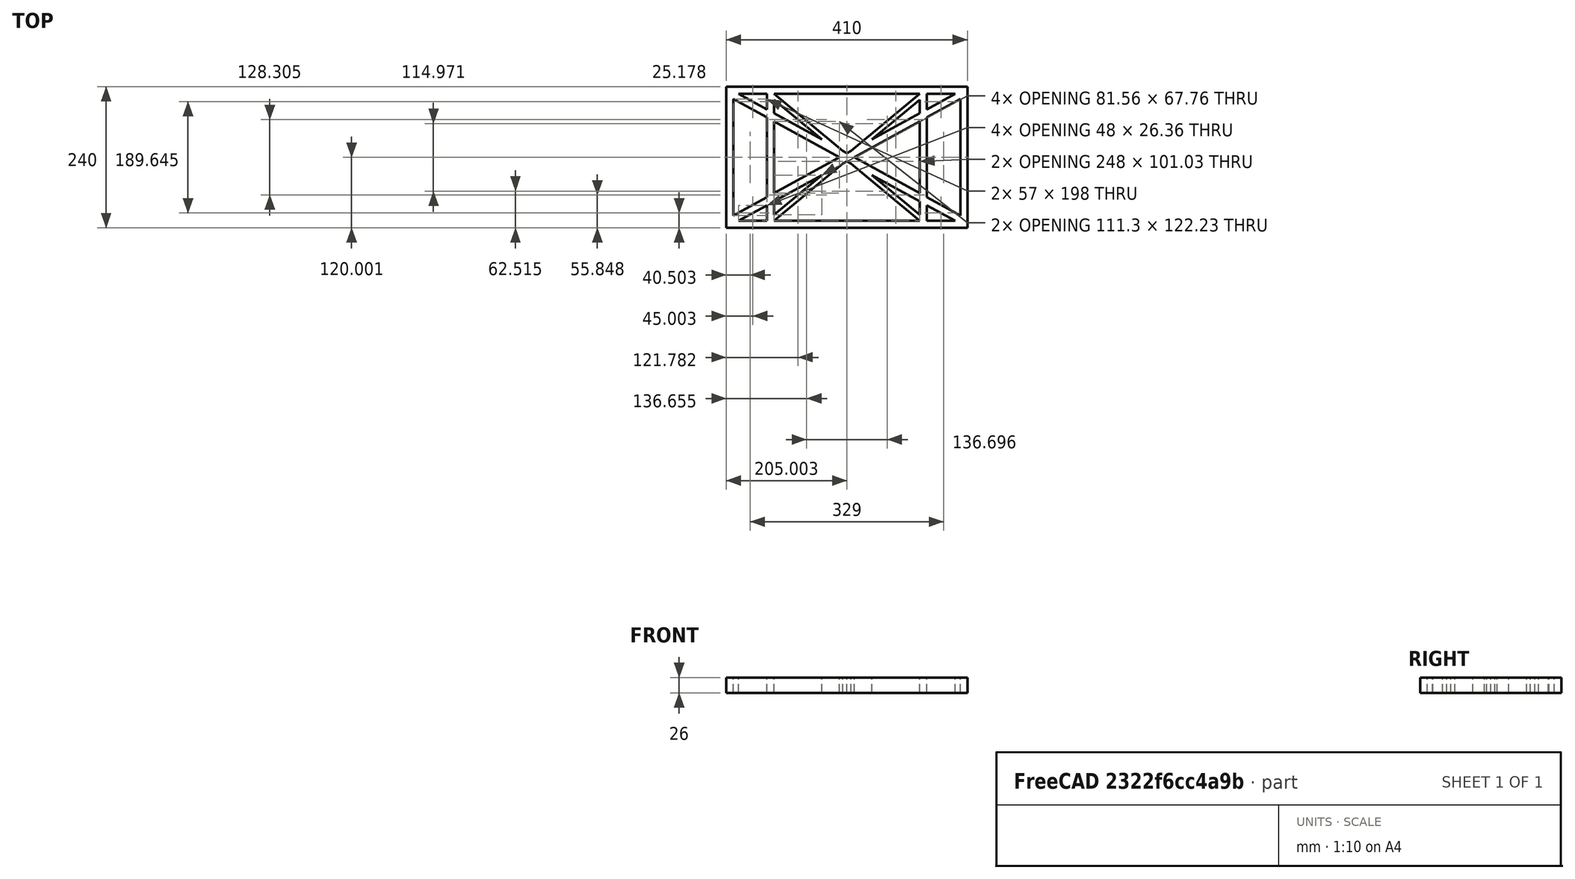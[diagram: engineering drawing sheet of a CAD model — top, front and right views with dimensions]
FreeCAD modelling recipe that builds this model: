
FCSTD DOCUMENT  (FreeCAD 0.19R0.19.2)
Label: laptopStand035
License: All rights reserved
LicenseURL: http://en.wikipedia.org/wiki/All_rights_reserved
objects: Sketcher::SketchObject×2, Part::Extrusion×1
note: 3 computed .brp shape members not serialized (recipe doc carries the construction recipe); baked Part::Feature solids carry a one-line shape summary decoded from their .brp

FEATURE [Sketcher::SketchObject] Sketch
  FullyConstrained = true
  sketch-geometry (52):
    g0: LineSegment StartX=-22.9272 StartY=136.221 StartZ=0 EndX=-22.9272 EndY=-103.779 EndZ=0
    g1: LineSegment StartX=-22.9272 StartY=136.221 StartZ=0 EndX=387.073 EndY=136.221 EndZ=0
    g2: LineSegment StartX=-22.9272 StartY=-103.779 StartZ=0 EndX=387.073 EndY=-103.779 EndZ=0
    g3: LineSegment StartX=387.073 StartY=136.221 StartZ=0 EndX=387.073 EndY=-103.779 EndZ=0
    g4: LineSegment StartX=375.073 StartY=115.221 StartZ=0 EndX=318.073 EndY=83.9235 EndZ=0
    g5: LineSegment StartX=-10.9272 StartY=-82.7794 StartZ=0 EndX=46.0728 EndY=-51.4823 EndZ=0
    g6: LineSegment StartX=-1.92719 StartY=124.221 StartZ=0 EndX=46.0728 EndY=97.8651 EndZ=0
    g7: LineSegment StartX=366.073 StartY=-91.7794 StartZ=0 EndX=318.073 EndY=-65.424 EndZ=0
    g8: LineSegment StartX=-10.9272 StartY=115.221 StartZ=0 EndX=-10.9272 EndY=-82.7794 EndZ=0
    g9: LineSegment StartX=375.073 StartY=-82.7794 StartZ=0 EndX=375.073 EndY=115.221 EndZ=0
    g10: LineSegment StartX=-1.92719 StartY=-91.7794 StartZ=0 EndX=46.0728 EndY=-91.7794 EndZ=0
    g11: LineSegment StartX=318.073 StartY=124.221 StartZ=0 EndX=366.073 EndY=124.221 EndZ=0
    g12: LineSegment StartX=306.073 StartY=-81.8102 StartZ=0 EndX=224.513 EndY=-14.0532 EndZ=0
    g13: LineSegment StartX=58.0728 StartY=114.251 StartZ=0 EndX=139.632 EndY=46.4944 EndZ=0
    g14: LineSegment StartX=306.073 StartY=124.221 StartZ=0 EndX=189.124 EndY=27.0628 EndZ=0
    g15: LineSegment StartX=58.0728 StartY=-91.7794 StartZ=0 EndX=175.022 EndY=5.37834 EndZ=0
    g16: LineSegment StartX=46.0728 StartY=124.221 StartZ=0 EndX=46.0728 EndY=97.8651 EndZ=0
    g17: LineSegment StartX=58.0728 StartY=-81.8102 StartZ=0 EndX=58.0728 EndY=-58.8351 EndZ=0
    g18: LineSegment StartX=318.073 StartY=124.221 StartZ=0 EndX=318.073 EndY=97.8651 EndZ=0
    g19: LineSegment StartX=306.073 StartY=114.251 StartZ=0 EndX=306.073 EndY=91.2763 EndZ=0
    g20: LineSegment StartX=182.073 StartY=23.1914 StartZ=0 EndX=189.124 EndY=27.0628 EndZ=0
    g21: LineSegment StartX=182.073 StartY=9.24976 StartZ=0 EndX=175.022 EndY=5.37834 EndZ=0
    g22: LineSegment StartX=224.513 StartY=46.4944 StartZ=0 EndX=306.073 EndY=114.251 EndZ=0
    g23: LineSegment StartX=175.022 StartY=27.0628 StartZ=0 EndX=58.0728 EndY=124.221 EndZ=0
    g24: LineSegment StartX=169.377 StartY=16.2206 StartZ=0 EndX=58.0728 EndY=77.3346 EndZ=0
    g25: LineSegment StartX=139.632 StartY=-14.0532 StartZ=0 EndX=58.0728 EndY=-81.8102 EndZ=0
    g26: LineSegment StartX=194.768 StartY=16.2206 StartZ=0 EndX=306.073 EndY=-44.8935 EndZ=0
    g27: LineSegment StartX=224.513 StartY=46.4944 StartZ=0 EndX=306.073 EndY=91.2763 EndZ=0
    g28: LineSegment StartX=175.022 StartY=27.0628 StartZ=0 EndX=182.073 EndY=23.1914 EndZ=0
    g29: LineSegment StartX=139.632 StartY=-14.0532 StartZ=0 EndX=58.0728 EndY=-58.8351 EndZ=0
    g30: LineSegment StartX=189.124 StartY=5.37834 StartZ=0 EndX=182.073 EndY=9.24976 EndZ=0
    g31: LineSegment StartX=189.124 StartY=5.37834 StartZ=0 EndX=306.073 EndY=-91.7794 EndZ=0
    g32: LineSegment StartX=306.073 StartY=77.3346 StartZ=0 EndX=306.073 EndY=-44.8935 EndZ=0
    g33: LineSegment StartX=318.073 StartY=83.9235 StartZ=0 EndX=318.073 EndY=-51.4823 EndZ=0
    g34: LineSegment StartX=318.073 StartY=97.8651 StartZ=0 EndX=366.073 EndY=124.221 EndZ=0
    g35: LineSegment StartX=306.073 StartY=77.3346 StartZ=0 EndX=194.768 EndY=16.2206 EndZ=0
    g36: LineSegment StartX=306.073 StartY=-58.8351 StartZ=0 EndX=224.513 EndY=-14.0532 EndZ=0
    g37: LineSegment StartX=306.073 StartY=-58.8351 StartZ=0 EndX=306.073 EndY=-81.8102 EndZ=0
    g38: LineSegment StartX=318.073 StartY=-51.4823 StartZ=0 EndX=375.073 EndY=-82.7794 EndZ=0
    g39: LineSegment StartX=318.073 StartY=-65.424 StartZ=0 EndX=318.073 EndY=-91.7794 EndZ=0
    g40: LineSegment StartX=306.073 StartY=124.221 StartZ=0 EndX=58.0728 EndY=124.221 EndZ=0
    g41: LineSegment StartX=318.073 StartY=-91.7794 StartZ=0 EndX=366.073 EndY=-91.7794 EndZ=0
    g42: LineSegment StartX=58.0728 StartY=-91.7794 StartZ=0 EndX=306.073 EndY=-91.7794 EndZ=0
    g43: LineSegment StartX=58.0728 StartY=-44.8935 StartZ=0 EndX=58.0728 EndY=77.3346 EndZ=0
    g44: LineSegment StartX=46.0728 StartY=-65.424 StartZ=0 EndX=-1.92719 EndY=-91.7794 EndZ=0
    g45: LineSegment StartX=46.0728 StartY=-65.424 StartZ=0 EndX=46.0728 EndY=-91.7794 EndZ=0
    g46: LineSegment StartX=58.0728 StartY=-44.8935 StartZ=0 EndX=169.377 EndY=16.2206 EndZ=0
    g47: LineSegment StartX=58.0728 StartY=91.2763 StartZ=0 EndX=58.0728 EndY=114.251 EndZ=0
    g48: LineSegment StartX=46.0728 StartY=83.9235 StartZ=0 EndX=46.0728 EndY=-51.4823 EndZ=0
    g49: LineSegment StartX=46.0728 StartY=124.221 StartZ=0 EndX=-1.92719 EndY=124.221 EndZ=0
    g50: LineSegment StartX=58.0728 StartY=91.2763 StartZ=0 EndX=139.632 EndY=46.4944 EndZ=0
    g51: LineSegment StartX=46.0728 StartY=83.9235 StartZ=0 EndX=-10.9272 EndY=115.221 EndZ=0
  constraints (102):
    c: Vertical(g0)
    c: Distance(g0) = 240
    c: Horizontal(g1)
    c: Distance(g1) = 410
    c: Coincident(g1,g0)
    c: Coincident(g2,g0)
    c: Horizontal(g2)
    c: Coincident(g3,g1)
    c: Vertical(g3)
    c: Coincident(g2,g3)
    c: Block(g1)
    c: Horizontal(g10)
    c: Horizontal(g11)
    c: PointOnObject(g35,g6)
    c: Coincident(g28,g20)
    c: Coincident(g30,g21)
    c: Tangent(g7,g24)
    c: PointOnObject(g24,g5)
    c: PointOnObject(g26,g4)
    c: Coincident(g20,g14)
    c: Tangent(g20,g27)
    c: Coincident(g50,g13)
    c: Coincident(g28,g23)
    c: Coincident(g22,g27)
    c: Coincident(g21,g15)
    c: Coincident(g29,g25)
    c: Tangent(g21,g29)
    c: Coincident(g36,g12)
    c: Coincident(g31,g30)
    c: Coincident(g22,g19)
    c: Tangent(g19,g32)
    c: Tangent(g18,g33)
    c: Coincident(g27,g19)
    c: Tangent(g27,g34)
    c: Coincident(g4,g33)
    c: Coincident(g35,g32)
    c: Tangent(g4,g35)
    c: Coincident(g37,g12)
    c: Tangent(g7,g36)
    c: Tangent(g32,g37)
    c: Coincident(g26,g32)
    c: Tangent(g26,g38)
    c: Coincident(g33,g38)
    c: Coincident(g39,g7)
    c: Tangent(g33,g39)
    c: Coincident(g25,g17)
    c: Tangent(g17,g43)
    c: Coincident(g29,g17)
    c: Tangent(g29,g44)
    c: Coincident(g45,g44)
    c: Tangent(g16,g45)
    c: Coincident(g5,g48)
    c: Coincident(g46,g43)
    c: Tangent(g5,g46)
    c: Tangent(g43,g47)
    c: Tangent(g16,g48)
    c: Coincident(g13,g47)
    c: PointOnObject(g40,g23)
    c: Tangent(g40,g49)
    c: Coincident(g6,g16)
    c: Coincident(g50,g47)
    c: Tangent(g6,g50)
    c: Coincident(g24,g43)
    c: Coincident(g51,g48)
    c: Tangent(g24,g51)
    c: Block(g23)
    c: Block(g14)
    c: Block(g20)
    c: Block(g40)
    c: Block(g18)
    c: Block(g34)
    c: Block(g4)
    c: Block(g38)
    c: Block(g9)
    c: Block(g36)
    c: Block(g37)
    c: Block(g7)
    c: Block(g39)
    c: Block(g22)
    c: Block(g31)
    c: Block(g42)
    c: Block(g21)
    c: Block(g15)
    c: Block(g29)
    c: Block(g25)
    c: Block(g45)
    c: Block(g44)
    c: Block(g5)
    c: Block(g8)
    c: Block(g51)
    c: Block(g6)
    c: Block(g16)
    c: Block(g13)
    c: Block(g47)
    c: Block(g35)
    c: Block(g32)
    c: Block(g24)
    c: Block(g46)
    c: Block(g49)
    c: Block(g11)
    c: Block(g41)
    c: Block(g10)
FEATURE [Part::Extrusion] Extrude
  Base = -> Sketch
  Dir = (0,0,1)
  DirMode = 2
  FaceMakerClass = Part::FaceMakerBullseye
  LengthFwd = 26
  LengthRev = 0
  Solid = true
  Symmetric = false
FEATURE [Sketcher::SketchObject] Sketch001
  FullyConstrained = true
  MapMode = 4
  Placement = pos=(0,0,0) rot=(0.57735,0.57735,0.57735;2.0944rad)
  Support = -> [Sketch]
  sketch-geometry (46):
    g0: BSplineCurve PolesCount=3 KnotsCount=2 Degree=2 IsPeriodic=0
    g1: ArcOfCircle CenterX=73.122 CenterY=-32.2909 CenterZ=0 NormalX=0 NormalY=0 NormalZ=1 AngleXU=0 Radius=13 StartAngle=5.92268 EndAngle=9.06428
    g2: LineSegment StartX=85.2864 StartY=-36.8765 StartZ=0 EndX=78.9505 EndY=-53.7246 EndZ=0
    g3: LineSegment StartX=60.9577 StartY=-27.7052 StartZ=0 EndX=54.6191 EndY=-44.5532 EndZ=0
    g4: ArcOfCircle CenterX=66.7816 CenterY=-49.1439 CenterZ=0 NormalX=0 NormalY=0 NormalZ=1 AngleXU=0 Radius=13 StartAngle=2.78068 EndAngle=5.92131
    g5: ArcOfCircle CenterX=55.9263 CenterY=-78.1807 CenterZ=0 NormalX=0 NormalY=0 NormalZ=1 AngleXU=0 Radius=13 StartAngle=5.92268 EndAngle=9.06428
    g6: LineSegment StartX=68.0907 StartY=-82.7664 StartZ=0 EndX=61.7547 EndY=-99.6148 EndZ=0
    g7: ArcOfCircle CenterX=49.5884 CenterY=-95.0342 CenterZ=0 NormalX=0 NormalY=0 NormalZ=1 AngleXU=0 Radius=13 StartAngle=2.78068 EndAngle=5.92131
    g8: LineSegment StartX=43.7619 StartY=-73.595 StartZ=0 EndX=37.426 EndY=-90.4435 EndZ=0
    g9: ArcOfCircle CenterX=38.7206 CenterY=-124.067 CenterZ=0 NormalX=0 NormalY=0 NormalZ=1 AngleXU=0 Radius=13 StartAngle=5.92268 EndAngle=9.06428
    g10: LineSegment StartX=26.5562 StartY=-119.481 StartZ=0 EndX=20.2251 EndY=-136.329 EndZ=0
    g11: ArcOfCircle CenterX=32.3875 CenterY=-140.92 CenterZ=0 NormalX=0 NormalY=0 NormalZ=1 AngleXU=0 Radius=13 StartAngle=2.78068 EndAngle=5.92131
    g12: LineSegment StartX=50.885 StartY=-128.652 StartZ=0 EndX=44.549 EndY=-145.5 EndZ=0
    g13: ArcOfCircle CenterX=21.4715 CenterY=-169.934 CenterZ=0 NormalX=0 NormalY=0 NormalZ=1 AngleXU=0 Radius=13 StartAngle=5.92268 EndAngle=9.06428
    g14: LineSegment StartX=9.3071 StartY=-165.349 StartZ=0 EndX=2.97115 EndY=-182.197 EndZ=0
    g15: ArcOfCircle CenterX=15.1336 CenterY=-186.787 CenterZ=0 NormalX=0 NormalY=0 NormalZ=1 AngleXU=0 Radius=13 StartAngle=2.78068 EndAngle=5.92131
    g16: LineSegment StartX=33.6358 StartY=-174.52 StartZ=0 EndX=27.2999 EndY=-191.368 EndZ=0
    g17-g20: Circle x4 (B-spline internal-alignment scaffolding for g21; pole/knot coordinates omitted)
    g21: BSplineCurve PolesCount=4 KnotsCount=2 Degree=3 IsPeriodic=0
    g22: GeomPoint X=28.8094 Y=-19.0875 Z=0
    g23: GeomPoint X=47.0443 Y=-50.4712 Z=0
    g24: Circle CenterX=53.5586 CenterY=-23.2695 CenterZ=0 NormalX=0 NormalY=0 NormalZ=1 AngleXU=0 Radius=3.24518
    g25: Circle CenterX=-195.441 CenterY=-127.082 CenterZ=0 NormalX=0 NormalY=0 NormalZ=1 AngleXU=0 Radius=1
    g26: Circle CenterX=-8.24091 CenterY=-197.481 CenterZ=0 NormalX=0 NormalY=0 NormalZ=1 AngleXU=0 Radius=1
    g27: Circle CenterX=12.8789 CenterY=-141.321 CenterZ=0 NormalX=0 NormalY=0 NormalZ=1 AngleXU=0 Radius=1
    g28: BSplineCurve PolesCount=3 KnotsCount=2 Degree=2 IsPeriodic=0
    g29: GeomPoint X=-195.441 Y=-127.082 Z=0
    g30: GeomPoint X=12.8789 Y=-141.321 Z=0
    g31: Circle CenterX=-12.8016 CenterY=-179.036 CenterZ=0 NormalX=0 NormalY=0 NormalZ=1 AngleXU=0 Radius=10.5072
    g32: Circle CenterX=0.933922 CenterY=-166.43 CenterZ=0 NormalX=0 NormalY=0 NormalZ=1 AngleXU=0 Radius=3.26661
    g33: Circle CenterX=-33.5518 CenterY=-176.44 CenterZ=0 NormalX=0 NormalY=0 NormalZ=1 AngleXU=0 Radius=5.64388
    g34: Circle CenterX=-47.2366 CenterY=-173.859 CenterZ=0 NormalX=0 NormalY=0 NormalZ=1 AngleXU=0 Radius=3.01653
    g35: Circle CenterX=-56.2595 CenterY=-171.456 CenterZ=0 NormalX=0 NormalY=0 NormalZ=1 AngleXU=0 Radius=2.12826
    g36: ArcOfCircle CenterX=51.2151 CenterY=-198.473 CenterZ=0 NormalX=0 NormalY=0 NormalZ=1 AngleXU=0 Radius=20 StartAngle=2.78189 EndAngle=4.35269
    g37: LineSegment StartX=32.4951 StartY=-191.433 StartZ=0 EndX=94.6577 EndY=-26.1351 EndZ=0
    g38: LineSegment StartX=43.1192 StartY=-220.001 StartZ=0 EndX=-196.497 EndY=-129.89 EndZ=0
    g39: LineSegment StartX=43.1192 StartY=-220.001 StartZ=0 EndX=44.1752 EndY=-217.193 EndZ=0
    g40: LineSegment StartX=117.223 StartY=-19.0875 StartZ=0 EndX=117.223 EndY=-16.0875 EndZ=0
    g41: LineSegment StartX=117.223 StartY=-16.0875 StartZ=0 EndX=17.2232 EndY=-16.0875 EndZ=0
    g42: LineSegment StartX=17.2232 StartY=-16.0875 StartZ=0 EndX=17.2232 EndY=-19.0875 EndZ=0
    g43: LineSegment StartX=28.8094 StartY=-19.0875 StartZ=0 EndX=17.2232 EndY=-19.0875 EndZ=0
    g44: LineSegment StartX=47.0443 StartY=-50.4712 StartZ=0 EndX=12.8789 EndY=-141.321 EndZ=0
    g45: LineSegment StartX=-195.441 StartY=-127.082 StartZ=0 EndX=-196.497 EndY=-129.89 EndZ=0
  constraints (75):
    c: Block(g0)
    c: Block(g1)
    c: Distance(g2) = 18
    c: Coincident(g2,g1)
    c: Coincident(g3,g1)
    c: Block(g4)
    c: Coincident(g4,g3)
    c: Block(g3)
    c: Coincident(g6,g5)
    c: Coincident(g8,g5)
    c: Block(g7)
    c: Coincident(g7,g8)
    c: Block(g8)
    c: Block(g5)
    c: Block(g6)
    c: Coincident(g12,g9)
    c: Coincident(g10,g9)
    c: Block(g11)
    c: Coincident(g11,g10)
    c: Block(g10)
    c: Block(g9)
    c: Coincident(g16,g13)
    c: Coincident(g14,g13)
    c: Block(g15)
    c: Coincident(g15,g14)
    c: Block(g14)
    c: Block(g13)
    c: Distance(g16) = 18
    c: Block(g16)
    c: Block(g12)
    c: Block(g2)
    c: Weight(g17) = 1
    c: Equal(g17,g18)
    c: Equal(g17,g19)
    c: Equal(g17,g20)
    c: InternalAlignment(g17-g20 -> g21) x4
    c: InternalAlignment(g22,g21)
    c: InternalAlignment(g23,g21)
    c: Block(g24)
    c: Weight(g25) = 1
    c: Equal(g25,g26)
    c: Equal(g25,g27)
    c: InternalAlignment(g25,g28)
    c: InternalAlignment(g26,g28)
    c: InternalAlignment(g27,g28)
    c: InternalAlignment(g29,g28)
    c: InternalAlignment(g30,g28)
    c: Block(g28)
    c: Block(g31)
    c: Block(g32)
    c: Block(g33)
    c: Block(g34)
    c: Block(g35)
    c: Block(g36)
    c: Coincident(g37,g36)
    c: Coincident(g37,g0)
    c: Block(g21)
    c: Coincident(g39,g38)
    c: Coincident(g39,g36)
    c: Block(g39)
    c: Coincident(g40,g0)
    c: Vertical(g40)
    c: Coincident(g41,g40)
    c: Horizontal(g41)
    c: Coincident(g42,g41)
    c: Vertical(g42)
    c: Block(g41)
    c: Coincident(g43,g21)
    c: Coincident(g43,g42)
    c: Horizontal(g43)
    c: Coincident(g44,g21)
    c: Coincident(g44,g28)
    c: Coincident(g45,g28)
    c: Coincident(g45,g38)
    c: Block(g38)
